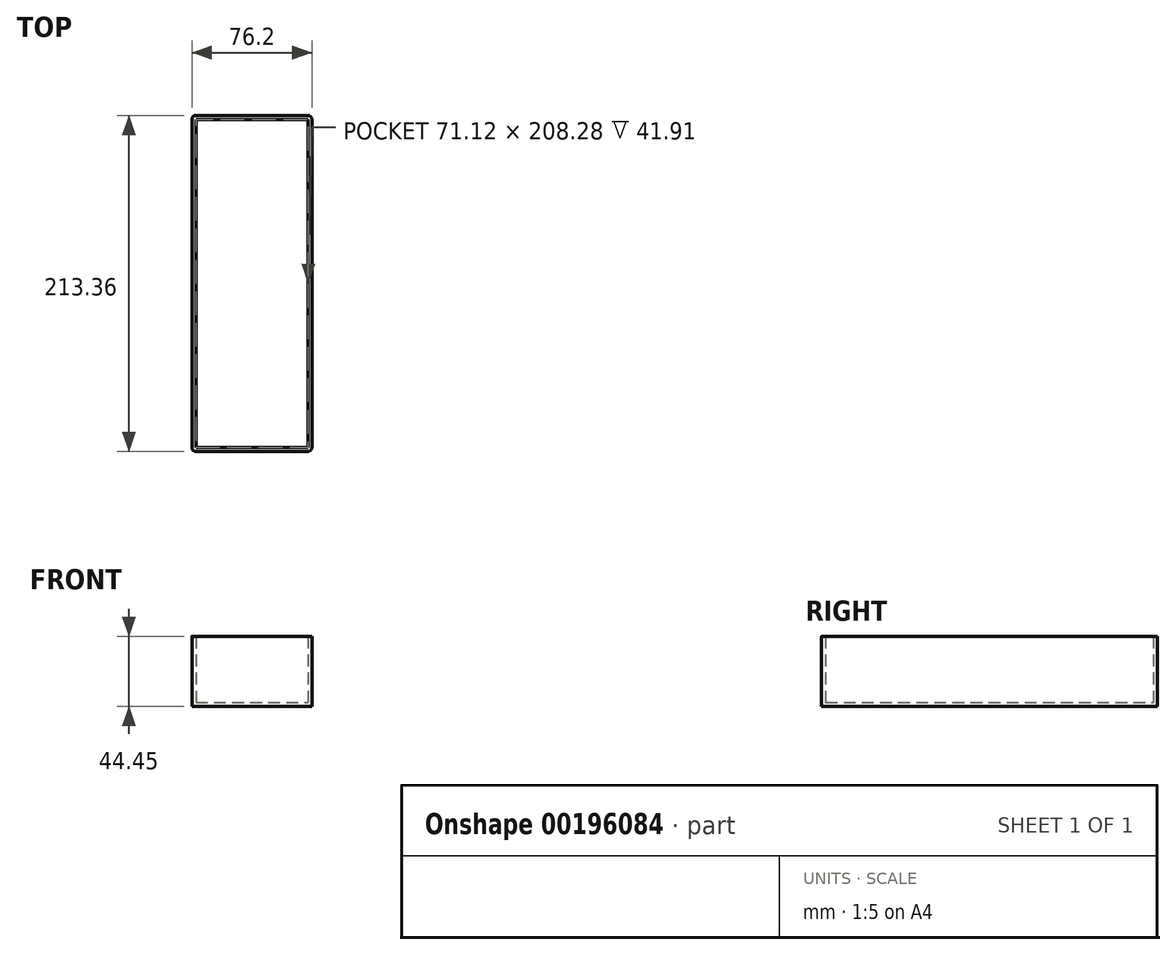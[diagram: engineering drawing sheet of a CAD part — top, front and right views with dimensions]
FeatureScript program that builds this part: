
annotation { "Feature Type Name" : "Feature", "Feature Type Description" : "" }
export const myFeature = defineFeature(function(context is Context, id is Id, definition is map)
    precondition{}
    {
        {
            var Q0;
            Q0=qCreatedBy(makeId("Top.planeOp"),FACE);
            var sketch = newSketch(context, id + "F0", { "sketchPlane" : qUnion([Q0])});
            skLineSegment(sketch, "E0.bottom", {"start": v(0, 0) * mm, "end": v(76.2, 0) * mm});
            skLineSegment(sketch, "E0.top", {"start": v(0, 213.36) * mm, "end": v(76.2, 213.36) * mm});
            skLineSegment(sketch, "E0.left", {"start": v(0, 0) * mm, "end": v(0, 213.36) * mm});
            skLineSegment(sketch, "E0.right", {"start": v(76.2, 0) * mm, "end": v(76.2, 213.36) * mm});
            skSolve(sketch);
        }
        {
            var Q0;
            Q0=makeQuery(id+"F0.imprint","IMPRINT",FACE,{"disambiguationData":[TD([[makeQuery(id+"F0.imprint","IMPRINT",EDGE,{"derivedFrom":sQuery(id+"F0.wireOp",EDGE,"E0.bottom")}),1.0]])]});
            extrude(context, id + "F1", {"entities" : qUnion([Q0]), "depth" : 44.45 * mm});
        }
        {
            var Q0;
            Q0=makeQuery(id+"F1.opExtrude","CAP_FACE",FACE,{"disambiguationData":[OSD([sQuery(id+"F0.wireOp",EDGE,"E0.bottom"),sQuery(id+"F0.wireOp",EDGE,"E0.top"),sQuery(id+"F0.wireOp",EDGE,"E0.left"),sQuery(id+"F0.wireOp",EDGE,"E0.right")])],"isStart":false});
            shell(context, id + "F2", {"entities" : qUnion([Q0]), "thickness" : 2.54 * mm});
        }
        {
            var Q0;
            Q0=makeQuery(id+"F1.opExtrude","SWEPT_EDGE",EDGE,{"disambiguationData":[OSD([sQuery(id+"F0.wireOp",EDGE,"E0.bottom"),sQuery(id+"F0.wireOp",EDGE,"E0.left")])]});
            var Q1;
            Q1=makeQuery(id+"F1.opExtrude","SWEPT_EDGE",EDGE,{"disambiguationData":[OSD([sQuery(id+"F0.wireOp",EDGE,"E0.bottom"),sQuery(id+"F0.wireOp",EDGE,"E0.right")])]});
            var Q2;
            Q2=makeQuery(id+"F1.opExtrude","SWEPT_EDGE",EDGE,{"disambiguationData":[OSD([sQuery(id+"F0.wireOp",EDGE,"E0.top"),sQuery(id+"F0.wireOp",EDGE,"E0.right")])]});
            var Q3;
            Q3=makeQuery(id+"F1.opExtrude","SWEPT_EDGE",EDGE,{"disambiguationData":[OSD([sQuery(id+"F0.wireOp",EDGE,"E0.top"),sQuery(id+"F0.wireOp",EDGE,"E0.left")])]});
            fillet(context, id + "F3", {"entities" : qUnion([Q0, Q1, Q2, Q3]), "radius" : 2.54 * mm, "tangentPropagation" : true, "allowEdgeOverflow" : false});
        }
    });
